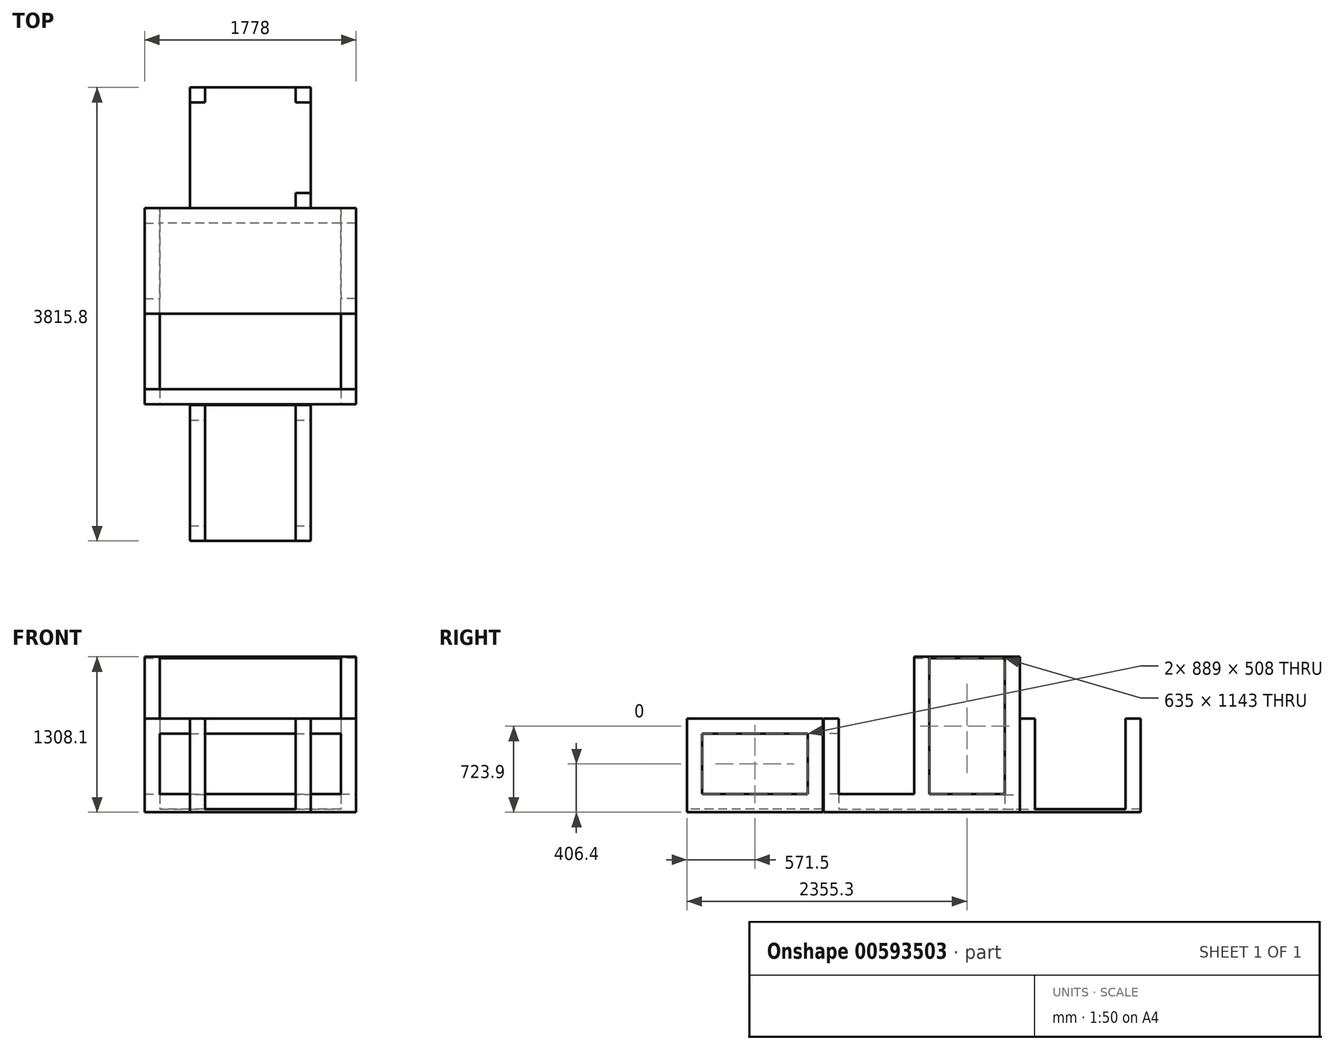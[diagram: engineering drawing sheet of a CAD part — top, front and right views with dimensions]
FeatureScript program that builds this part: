
annotation { "Feature Type Name" : "Feature", "Feature Type Description" : "" }
export const myFeature = defineFeature(function(context is Context, id is Id, definition is map)
    precondition{}
    {
        {
            var Q0;
            Q0=qCreatedBy(makeId("Top.planeOp"),FACE);
            var sketch = newSketch(context, id + "F0", { "sketchPlane" : qUnion([Q0])});
            skLineSegment(sketch, "E0.bottom", {"start": v(508, -571.5) * mm, "end": v(-508, -571.5) * mm});
            skLineSegment(sketch, "E0.top", {"start": v(508, 571.5) * mm, "end": v(-508, 571.5) * mm});
            skLineSegment(sketch, "E0.left", {"start": v(508, -571.5) * mm, "end": v(508, 571.5) * mm});
            skLineSegment(sketch, "E0.right", {"start": v(-508, -571.5) * mm, "end": v(-508, 571.5) * mm});
            skPoint(sketch, "E0.middle", {"position": v(0, 0) * mm});
            skLineSegment(sketch, "E1.bottom", {"start": v(-889, 577.3) * mm, "end": v(889, 577.3) * mm});
            skLineSegment(sketch, "E1.top", {"start": v(-889, 2228.3) * mm, "end": v(889, 2228.3) * mm});
            skLineSegment(sketch, "E1.left", {"start": v(-889, 577.3) * mm, "end": v(-889, 2228.3) * mm});
            skLineSegment(sketch, "E1.right", {"start": v(889, 577.3) * mm, "end": v(889, 2228.3) * mm});
            skSolve(sketch);
        }
        {
            var Q0;
            Q0=makeQuery(id+"F0.imprint","IMPRINT",FACE,{"disambiguationData":[TD([[makeQuery(id+"F0.imprint","IMPRINT",EDGE,{"derivedFrom":sQuery(id+"F0.wireOp",EDGE,"E1.bottom")}),1.0]])]});
            var sketch = newSketch(context, id + "F1", { "sketchPlane" : qUnion([Q0])});
            skLineSegment(sketch, "E2.bottom", {"start": v(-508, 2228.3) * mm, "end": v(508, 2228.3) * mm});
            skLineSegment(sketch, "E2.top", {"start": v(-508, 3244.3) * mm, "end": v(508, 3244.3) * mm});
            skLineSegment(sketch, "E2.left", {"start": v(-508, 2228.3) * mm, "end": v(-508, 3244.3) * mm});
            skLineSegment(sketch, "E2.right", {"start": v(508, 2228.3) * mm, "end": v(508, 3244.3) * mm});
            skSolve(sketch);
        }
        {
            var Q0;
            Q0=makeQuery(id+"F1.imprint","IMPRINT",FACE,{"disambiguationData":[TD([[makeQuery(id+"F1.imprint","IMPRINT",EDGE,{"derivedFrom":sQuery(id+"F1.wireOp",EDGE,"E2.bottom")}),1.0]])]});
            var Q1;
            Q1=makeQuery(id+"F0.imprint","IMPRINT",FACE,{"disambiguationData":[TD([[makeQuery(id+"F0.imprint","IMPRINT",EDGE,{"derivedFrom":sQuery(id+"F0.wireOp",EDGE,"E1.bottom")}),1.0]])]});
            var Q2;
            Q2=makeQuery(id+"F0.imprint","IMPRINT",FACE,{"disambiguationData":[TD([[makeQuery(id+"F0.imprint","IMPRINT",EDGE,{"derivedFrom":sQuery(id+"F0.wireOp",EDGE,"E0.bottom")}),-1.0]])]});
            extrude(context, id + "F2", {"entities" : qUnion([Q0, Q1, Q2]), "depth" : 25.4 * mm, "offsetDistance" : 25.4 * mm});
        }
        {
            var Q0;
            Q0=makeQuery(id+"F2.opExtrude","CAP_FACE",FACE,{"disambiguationData":[OSD([sQuery(id+"F0.wireOp",EDGE,"E0.bottom"),sQuery(id+"F0.wireOp",EDGE,"E0.top"),sQuery(id+"F0.wireOp",EDGE,"E0.left"),sQuery(id+"F0.wireOp",EDGE,"E0.right")])],"isStart":false});
            var sketch = newSketch(context, id + "F3", { "sketchPlane" : qUnion([Q0])});
            skLineSegment(sketch, "E3.bottom", {"start": v(-508, 571.5) * mm, "end": v(-381, 571.5) * mm});
            skLineSegment(sketch, "E3.top", {"start": v(-508, 444.5) * mm, "end": v(-381, 444.5) * mm});
            skLineSegment(sketch, "E3.left", {"start": v(-508, 571.5) * mm, "end": v(-508, 444.5) * mm});
            skLineSegment(sketch, "E3.right", {"start": v(-381, 571.5) * mm, "end": v(-381, 444.5) * mm});
            skLineSegment(sketch, "E4.bottom", {"start": v(508, 571.5) * mm, "end": v(381, 571.5) * mm});
            skLineSegment(sketch, "E4.top", {"start": v(508, 444.5) * mm, "end": v(381, 444.5) * mm});
            skLineSegment(sketch, "E4.left", {"start": v(508, 571.5) * mm, "end": v(508, 444.5) * mm});
            skLineSegment(sketch, "E4.right", {"start": v(381, 571.5) * mm, "end": v(381, 444.5) * mm});
            skSolve(sketch);
        }
        {
            var Q0;
            Q0=makeQuery(id+"F3.imprint","IMPRINT",FACE,{"disambiguationData":[TD([[makeQuery(id+"F3.imprint","IMPRINT",EDGE,{"derivedFrom":sQuery(id+"F3.wireOp",EDGE,"E4.bottom")}),1.0]])]});
            var Q1;
            Q1=makeQuery(id+"F3.imprint","IMPRINT",FACE,{"disambiguationData":[TD([[makeQuery(id+"F3.imprint","IMPRINT",EDGE,{"derivedFrom":sQuery(id+"F3.wireOp",EDGE,"E3.bottom")}),1.0]])]});
            extrude(context, id + "F4", {"entities" : qUnion([Q0, Q1]), "operationType" : NewBodyOperationType.ADD, "depth" : 762 * mm, "offsetDistance" : 25.4 * mm});
        }
        {
            var Q0;
            Q0=makeQuery(id+"F2.opExtrude","CAP_FACE",FACE,{"disambiguationData":[OSD([sQuery(id+"F0.wireOp",EDGE,"E1.bottom"),sQuery(id+"F0.wireOp",EDGE,"E1.top"),sQuery(id+"F0.wireOp",EDGE,"E1.left"),sQuery(id+"F0.wireOp",EDGE,"E1.right")])],"isStart":false});
            var sketch = newSketch(context, id + "F5", { "sketchPlane" : qUnion([Q0])});
            skLineSegment(sketch, "E5.bottom", {"start": v(889, 1339.3) * mm, "end": v(762, 1339.3) * mm});
            skLineSegment(sketch, "E5.top", {"start": v(889, 1466.3) * mm, "end": v(762, 1466.3) * mm});
            skLineSegment(sketch, "E5.left", {"start": v(889, 1339.3) * mm, "end": v(889, 1466.3) * mm});
            skLineSegment(sketch, "E5.right", {"start": v(762, 1339.3) * mm, "end": v(762, 1466.3) * mm});
            skLineSegment(sketch, "E6.bottom", {"start": v(-889, 1339.3) * mm, "end": v(-762, 1339.3) * mm});
            skLineSegment(sketch, "E6.top", {"start": v(-889, 1466.3) * mm, "end": v(-762, 1466.3) * mm});
            skLineSegment(sketch, "E6.left", {"start": v(-889, 1339.3) * mm, "end": v(-889, 1466.3) * mm});
            skLineSegment(sketch, "E6.right", {"start": v(-762, 1339.3) * mm, "end": v(-762, 1466.3) * mm});
            skLineSegment(sketch, "E7.bottom", {"start": v(-889, 2228.3) * mm, "end": v(-762, 2228.3) * mm});
            skLineSegment(sketch, "E7.top", {"start": v(-889, 2101.3) * mm, "end": v(-762, 2101.3) * mm});
            skLineSegment(sketch, "E7.left", {"start": v(-889, 2228.3) * mm, "end": v(-889, 2101.3) * mm});
            skLineSegment(sketch, "E7.right", {"start": v(-762, 2228.3) * mm, "end": v(-762, 2101.3) * mm});
            skLineSegment(sketch, "E8.bottom", {"start": v(889, 2228.3) * mm, "end": v(762, 2228.3) * mm});
            skLineSegment(sketch, "E8.top", {"start": v(889, 2101.3) * mm, "end": v(762, 2101.3) * mm});
            skLineSegment(sketch, "E8.left", {"start": v(889, 2228.3) * mm, "end": v(889, 2101.3) * mm});
            skLineSegment(sketch, "E8.right", {"start": v(762, 2228.3) * mm, "end": v(762, 2101.3) * mm});
            skSolve(sketch);
        }
        {
            var Q0;
            Q0=makeQuery(id+"F5.imprint","IMPRINT",FACE,{"disambiguationData":[TD([[makeQuery(id+"F5.imprint","IMPRINT",EDGE,{"derivedFrom":sQuery(id+"F5.wireOp",EDGE,"E5.bottom")}),-1.0]])]});
            var Q1;
            Q1=makeQuery(id+"F5.imprint","IMPRINT",FACE,{"disambiguationData":[TD([[makeQuery(id+"F5.imprint","IMPRINT",EDGE,{"derivedFrom":sQuery(id+"F5.wireOp",EDGE,"E6.bottom")}),1.0]])]});
            var Q2;
            Q2=makeQuery(id+"F5.imprint","IMPRINT",FACE,{"disambiguationData":[TD([[makeQuery(id+"F5.imprint","IMPRINT",EDGE,{"derivedFrom":sQuery(id+"F5.wireOp",EDGE,"E7.bottom")}),-1.0]])]});
            var Q3;
            Q3=makeQuery(id+"F5.imprint","IMPRINT",FACE,{"disambiguationData":[TD([[makeQuery(id+"F5.imprint","IMPRINT",EDGE,{"derivedFrom":sQuery(id+"F5.wireOp",EDGE,"E8.bottom")}),-1.0]])]});
            extrude(context, id + "F6", {"entities" : qUnion([Q0, Q1, Q2, Q3]), "operationType" : NewBodyOperationType.ADD, "depth" : 1270 * mm, "offsetDistance" : 25.4 * mm});
        }
        {
            var Q0;
            Q0=makeQuery(id+"F2.opExtrude","CAP_FACE",FACE,{"disambiguationData":[OSD([sQuery(id+"F1.wireOp",EDGE,"E2.bottom"),sQuery(id+"F1.wireOp",EDGE,"E2.top"),sQuery(id+"F1.wireOp",EDGE,"E2.left"),sQuery(id+"F1.wireOp",EDGE,"E2.right")])],"isStart":false});
            var sketch = newSketch(context, id + "F7", { "sketchPlane" : qUnion([Q0])});
            skLineSegment(sketch, "E9.bottom", {"start": v(-508, 3244.3) * mm, "end": v(-381, 3244.3) * mm});
            skLineSegment(sketch, "E9.top", {"start": v(-508, 3117.3) * mm, "end": v(-381, 3117.3) * mm});
            skLineSegment(sketch, "E9.left", {"start": v(-508, 3244.3) * mm, "end": v(-508, 3117.3) * mm});
            skLineSegment(sketch, "E9.right", {"start": v(-381, 3244.3) * mm, "end": v(-381, 3117.3) * mm});
            skLineSegment(sketch, "E10.bottom", {"start": v(508, 3244.3) * mm, "end": v(381, 3244.3) * mm});
            skLineSegment(sketch, "E10.top", {"start": v(508, 3117.3) * mm, "end": v(381, 3117.3) * mm});
            skLineSegment(sketch, "E10.left", {"start": v(508, 3244.3) * mm, "end": v(508, 3117.3) * mm});
            skLineSegment(sketch, "E10.right", {"start": v(381, 3244.3) * mm, "end": v(381, 3117.3) * mm});
            skSolve(sketch);
        }
        {
            var Q0;
            Q0=makeQuery(id+"F7.imprint","IMPRINT",FACE,{"disambiguationData":[TD([[makeQuery(id+"F7.imprint","IMPRINT",EDGE,{"derivedFrom":sQuery(id+"F7.wireOp",EDGE,"E10.bottom")}),-1.0]])]});
            var Q1;
            Q1=makeQuery(id+"F7.imprint","IMPRINT",FACE,{"disambiguationData":[TD([[makeQuery(id+"F7.imprint","IMPRINT",EDGE,{"derivedFrom":sQuery(id+"F7.wireOp",EDGE,"E9.bottom")}),-1.0]])]});
            extrude(context, id + "F8", {"entities" : qUnion([Q0, Q1]), "operationType" : NewBodyOperationType.ADD, "depth" : 762 * mm, "offsetDistance" : 25.4 * mm});
        }
        {
            var Q0;
            Q0=makeQuery(id+"F2.opExtrude","CAP_FACE",FACE,{"disambiguationData":[OSD([sQuery(id+"F1.wireOp",EDGE,"E2.bottom"),sQuery(id+"F1.wireOp",EDGE,"E2.top"),sQuery(id+"F1.wireOp",EDGE,"E2.left"),sQuery(id+"F1.wireOp",EDGE,"E2.right")])],"isStart":false});
            var sketch = newSketch(context, id + "F9", { "sketchPlane" : qUnion([Q0])});
            skLineSegment(sketch, "E11.bottom", {"start": v(-508, 2228.3) * mm, "end": v(-381, 2228.3) * mm});
            skLineSegment(sketch, "E11.top", {"start": v(-508, 2355.3) * mm, "end": v(-381, 2355.3) * mm});
            skLineSegment(sketch, "E11.left", {"start": v(-508, 2228.3) * mm, "end": v(-508, 2355.3) * mm});
            skLineSegment(sketch, "E11.right", {"start": v(-381, 2228.3) * mm, "end": v(-381, 2355.3) * mm});
            skLineSegment(sketch, "E12.bottom", {"start": v(508, 2228.3) * mm, "end": v(381, 2228.3) * mm});
            skLineSegment(sketch, "E12.top", {"start": v(508, 2355.3) * mm, "end": v(381, 2355.3) * mm});
            skLineSegment(sketch, "E12.left", {"start": v(508, 2228.3) * mm, "end": v(508, 2355.3) * mm});
            skLineSegment(sketch, "E12.right", {"start": v(381, 2228.3) * mm, "end": v(381, 2355.3) * mm});
            skSolve(sketch);
        }
        {
            var Q0;
            Q0=makeQuery(id+"F9.imprint","IMPRINT",FACE,{"disambiguationData":[TD([[makeQuery(id+"F9.imprint","IMPRINT",EDGE,{"derivedFrom":sQuery(id+"F9.wireOp",EDGE,"E11.bottom")}),1.0]])]});
            var sketch = newSketch(context, id + "F10", { "sketchPlane" : qUnion([Q0])});
            skSolve(sketch);
        }
        {
            var Q0;
            Q0 = qSketchRegion(id + "F10", true);
            var Q1;
            Q1=makeQuery(id+"F9.imprint","IMPRINT",FACE,{"disambiguationData":[TD([[makeQuery(id+"F9.imprint","IMPRINT",EDGE,{"derivedFrom":sQuery(id+"F9.wireOp",EDGE,"E12.bottom")}),1.0]])]});
            var Q2;
            Q2=makeQuery(id+"F10.imprint","IMPRINT",FACE,{"disambiguationData":[TD([[makeQuery(id+"F10.imprint","IMPRINT",EDGE,{"derivedFrom":makeQuery(id+"F9.imprint","IMPRINT",EDGE,{"derivedFrom":sQuery(id+"F9.wireOp",EDGE,"E11.bottom")})}),1.0]])]});
            extrude(context, id + "F11", {"entities" : qUnion([Q0, Q1, Q2]), "operationType" : NewBodyOperationType.ADD, "depth" : 762 * mm, "offsetDistance" : 25.4 * mm});
        }
        {
            var Q0;
            Q0=makeQuery(id+"F2.opExtrude","CAP_FACE",FACE,{"disambiguationData":[OSD([sQuery(id+"F0.wireOp",EDGE,"E0.bottom"),sQuery(id+"F0.wireOp",EDGE,"E0.top"),sQuery(id+"F0.wireOp",EDGE,"E0.left"),sQuery(id+"F0.wireOp",EDGE,"E0.right")])],"isStart":false});
            var sketch = newSketch(context, id + "F12", { "sketchPlane" : qUnion([Q0])});
            skLineSegment(sketch, "E13.bottom", {"start": v(-508, -571.5) * mm, "end": v(-381, -571.5) * mm});
            skLineSegment(sketch, "E13.top", {"start": v(-508, -444.5) * mm, "end": v(-381, -444.5) * mm});
            skLineSegment(sketch, "E13.left", {"start": v(-508, -571.5) * mm, "end": v(-508, -444.5) * mm});
            skLineSegment(sketch, "E13.right", {"start": v(-381, -571.5) * mm, "end": v(-381, -444.5) * mm});
            skLineSegment(sketch, "E14.bottom", {"start": v(508, -571.5) * mm, "end": v(381, -571.5) * mm});
            skLineSegment(sketch, "E14.top", {"start": v(508, -444.5) * mm, "end": v(381, -444.5) * mm});
            skLineSegment(sketch, "E14.left", {"start": v(508, -571.5) * mm, "end": v(508, -444.5) * mm});
            skLineSegment(sketch, "E14.right", {"start": v(381, -571.5) * mm, "end": v(381, -444.5) * mm});
            skSolve(sketch);
        }
        {
            var Q0;
            Q0=makeQuery(id+"F12.imprint","IMPRINT",FACE,{"disambiguationData":[TD([[makeQuery(id+"F12.imprint","IMPRINT",EDGE,{"derivedFrom":sQuery(id+"F12.wireOp",EDGE,"E13.bottom")}),-1.0]])]});
            var Q1;
            Q1=makeQuery(id+"F12.imprint","IMPRINT",FACE,{"disambiguationData":[TD([[makeQuery(id+"F12.imprint","IMPRINT",EDGE,{"derivedFrom":sQuery(id+"F12.wireOp",EDGE,"E14.bottom")}),-1.0]])]});
            extrude(context, id + "F13", {"entities" : qUnion([Q0, Q1]), "operationType" : NewBodyOperationType.ADD, "depth" : 762 * mm, "offsetDistance" : 25.4 * mm});
        }
        {
            var Q0;
            Q0=makeQuery(id+"F2.opExtrude","CAP_FACE",FACE,{"disambiguationData":[OSD([sQuery(id+"F0.wireOp",EDGE,"E1.bottom"),sQuery(id+"F0.wireOp",EDGE,"E1.top"),sQuery(id+"F0.wireOp",EDGE,"E1.left"),sQuery(id+"F0.wireOp",EDGE,"E1.right")])],"isStart":false});
            var sketch = newSketch(context, id + "F14", { "sketchPlane" : qUnion([Q0])});
            skLineSegment(sketch, "E15.bottom", {"start": v(-889, 577.3) * mm, "end": v(-762, 577.3) * mm});
            skLineSegment(sketch, "E15.top", {"start": v(-889, 704.3) * mm, "end": v(-762, 704.3) * mm});
            skLineSegment(sketch, "E15.left", {"start": v(-889, 577.3) * mm, "end": v(-889, 704.3) * mm});
            skLineSegment(sketch, "E15.right", {"start": v(-762, 577.3) * mm, "end": v(-762, 704.3) * mm});
            skLineSegment(sketch, "E16.bottom", {"start": v(889, 577.3) * mm, "end": v(762, 577.3) * mm});
            skLineSegment(sketch, "E16.top", {"start": v(889, 704.3) * mm, "end": v(762, 704.3) * mm});
            skLineSegment(sketch, "E16.left", {"start": v(889, 577.3) * mm, "end": v(889, 704.3) * mm});
            skLineSegment(sketch, "E16.right", {"start": v(762, 577.3) * mm, "end": v(762, 704.3) * mm});
            skSolve(sketch);
        }
        {
            var Q0;
            Q0=makeQuery(id+"F14.imprint","IMPRINT",FACE,{"disambiguationData":[TD([[makeQuery(id+"F14.imprint","IMPRINT",EDGE,{"derivedFrom":sQuery(id+"F14.wireOp",EDGE,"E15.bottom")}),1.0]])]});
            var Q1;
            Q1=makeQuery(id+"F14.imprint","IMPRINT",FACE,{"disambiguationData":[TD([[makeQuery(id+"F14.imprint","IMPRINT",EDGE,{"derivedFrom":sQuery(id+"F14.wireOp",EDGE,"E16.bottom")}),1.0]])]});
            extrude(context, id + "F15", {"entities" : qUnion([Q0, Q1]), "operationType" : NewBodyOperationType.ADD, "depth" : 762 * mm, "offsetDistance" : 25.4 * mm});
        }
        {
            var Q0;
            Q0=makeQuery(id+"F15.opExtrude","SWEPT_FACE",FACE,{"disambiguationData":[OSD([sQuery(id+"F14.wireOp",EDGE,"E16.right")])]});
            var sketch = newSketch(context, id + "F16", { "sketchPlane" : qUnion([Q0])});
            skLineSegment(sketch, "E17.bottom", {"start": v(-704.3, 787.4) * mm, "end": v(-577.3, 787.4) * mm});
            skLineSegment(sketch, "E17.top", {"start": v(-704.3, 660.4) * mm, "end": v(-577.3, 660.4) * mm});
            skLineSegment(sketch, "E17.left", {"start": v(-704.3, 787.4) * mm, "end": v(-704.3, 660.4) * mm});
            skLineSegment(sketch, "E17.right", {"start": v(-577.3, 787.4) * mm, "end": v(-577.3, 660.4) * mm});
            skSolve(sketch);
        }
        {
            var Q0;
            Q0=makeQuery(id+"F16.imprint","IMPRINT",FACE,{"disambiguationData":[TD([[makeQuery(id+"F16.imprint","IMPRINT",EDGE,{"derivedFrom":sQuery(id+"F16.wireOp",EDGE,"E17.bottom")}),1.0]])]});
            extrude(context, id + "F17", {"entities" : qUnion([Q0]), "operationType" : NewBodyOperationType.ADD, "depth" : 1524 * mm, "offsetDistance" : 25.4 * mm});
        }
        {
            var Q0;
            Q0=makeQuery(id+"F4.opExtrude","SWEPT_FACE",FACE,{"disambiguationData":[OSD([sQuery(id+"F3.wireOp",EDGE,"E3.top")])]});
            var sketch = newSketch(context, id + "F18", { "sketchPlane" : qUnion([Q0])});
            skLineSegment(sketch, "E18.bottom", {"start": v(-508, 787.4) * mm, "end": v(-381, 787.4) * mm});
            skLineSegment(sketch, "E18.top", {"start": v(-508, 660.4) * mm, "end": v(-381, 660.4) * mm});
            skLineSegment(sketch, "E18.left", {"start": v(-508, 787.4) * mm, "end": v(-508, 660.4) * mm});
            skLineSegment(sketch, "E18.right", {"start": v(-381, 787.4) * mm, "end": v(-381, 660.4) * mm});
            skLineSegment(sketch, "E19.bottom", {"start": v(381, 787.4) * mm, "end": v(508, 787.4) * mm});
            skLineSegment(sketch, "E19.top", {"start": v(381, 660.4) * mm, "end": v(508, 660.4) * mm});
            skLineSegment(sketch, "E19.left", {"start": v(381, 787.4) * mm, "end": v(381, 660.4) * mm});
            skLineSegment(sketch, "E19.right", {"start": v(508, 787.4) * mm, "end": v(508, 660.4) * mm});
            skSolve(sketch);
        }
        {
            var Q0;
            Q0=makeQuery(id+"F18.imprint","IMPRINT",FACE,{"disambiguationData":[TD([[makeQuery(id+"F18.imprint","IMPRINT",EDGE,{"derivedFrom":sQuery(id+"F18.wireOp",EDGE,"E19.bottom")}),-1.0]])]});
            var Q1;
            Q1=makeQuery(id+"F18.imprint","IMPRINT",FACE,{"disambiguationData":[TD([[makeQuery(id+"F18.imprint","IMPRINT",EDGE,{"derivedFrom":sQuery(id+"F18.wireOp",EDGE,"E18.bottom")}),-1.0]])]});
            extrude(context, id + "F19", {"entities" : qUnion([Q0, Q1]), "operationType" : NewBodyOperationType.ADD, "depth" : 889 * mm, "offsetDistance" : 25.4 * mm});
        }
        {
            var Q0;
            Q0=makeQuery(id+"F4.opExtrude","SWEPT_FACE",FACE,{"disambiguationData":[OSD([sQuery(id+"F3.wireOp",EDGE,"E3.top")])]});
            var sketch = newSketch(context, id + "F20", { "sketchPlane" : qUnion([Q0])});
            skLineSegment(sketch, "E20.bottom", {"start": v(-508, 25.4) * mm, "end": v(-381, 25.4) * mm});
            skLineSegment(sketch, "E20.top", {"start": v(-508, 152.4) * mm, "end": v(-381, 152.4) * mm});
            skLineSegment(sketch, "E20.left", {"start": v(-508, 25.4) * mm, "end": v(-508, 152.4) * mm});
            skLineSegment(sketch, "E20.right", {"start": v(-381, 25.4) * mm, "end": v(-381, 152.4) * mm});
            skLineSegment(sketch, "E21.bottom", {"start": v(381, 152.4) * mm, "end": v(508, 152.4) * mm});
            skLineSegment(sketch, "E21.top", {"start": v(381, 25.4) * mm, "end": v(508, 25.4) * mm});
            skLineSegment(sketch, "E21.left", {"start": v(381, 152.4) * mm, "end": v(381, 25.4) * mm});
            skLineSegment(sketch, "E21.right", {"start": v(508, 152.4) * mm, "end": v(508, 25.4) * mm});
            skSolve(sketch);
        }
        {
            var Q0;
            Q0=makeQuery(id+"F20.imprint","IMPRINT",FACE,{"disambiguationData":[TD([[makeQuery(id+"F20.imprint","IMPRINT",EDGE,{"derivedFrom":sQuery(id+"F20.wireOp",EDGE,"E20.bottom")}),1.0]])]});
            var Q1;
            Q1=makeQuery(id+"F20.imprint","IMPRINT",FACE,{"disambiguationData":[TD([[makeQuery(id+"F20.imprint","IMPRINT",EDGE,{"derivedFrom":sQuery(id+"F20.wireOp",EDGE,"E21.bottom")}),-1.0]])]});
            extrude(context, id + "F21", {"entities" : qUnion([Q0, Q1]), "operationType" : NewBodyOperationType.ADD, "depth" : 889 * mm, "offsetDistance" : 25.4 * mm});
        }
        {
            var Q0;
            Q0=makeQuery(id+"F2.opExtrude","CAP_FACE",FACE,{"disambiguationData":[OSD([sQuery(id+"F0.wireOp",EDGE,"E1.bottom"),sQuery(id+"F0.wireOp",EDGE,"E1.top"),sQuery(id+"F0.wireOp",EDGE,"E1.left"),sQuery(id+"F0.wireOp",EDGE,"E1.right")])],"isStart":false});
            var sketch = newSketch(context, id + "F22", { "sketchPlane" : qUnion([Q0])});
            skLineSegment(sketch, "E22.bottom", {"start": v(-762, 2101.3) * mm, "end": v(-889, 2101.3) * mm});
            skLineSegment(sketch, "E22.top", {"start": v(-762, 1466.3) * mm, "end": v(-889, 1466.3) * mm});
            skLineSegment(sketch, "E22.left", {"start": v(-762, 2101.3) * mm, "end": v(-762, 1466.3) * mm});
            skLineSegment(sketch, "E22.right", {"start": v(-889, 2101.3) * mm, "end": v(-889, 1466.3) * mm});
            skLineSegment(sketch, "E23.bottom", {"start": v(-762, 1339.3) * mm, "end": v(-889.9, 1339.3) * mm});
            skLineSegment(sketch, "E23.top", {"start": v(-762, 704.3) * mm, "end": v(-889.9, 704.3) * mm});
            skLineSegment(sketch, "E23.left", {"start": v(-762, 1339.3) * mm, "end": v(-762, 704.3) * mm});
            skLineSegment(sketch, "E23.right", {"start": v(-889.9, 1339.3) * mm, "end": v(-889.9, 704.3) * mm});
            skLineSegment(sketch, "E24.bottom", {"start": v(762, 1339.29) * mm, "end": v(889, 1339.29) * mm});
            skLineSegment(sketch, "E24.top", {"start": v(762, 704.3) * mm, "end": v(889, 704.3) * mm});
            skLineSegment(sketch, "E24.left", {"start": v(762, 1339.29) * mm, "end": v(762, 704.3) * mm});
            skLineSegment(sketch, "E24.right", {"start": v(889, 1339.29) * mm, "end": v(889, 704.3) * mm});
            skLineSegment(sketch, "E25.bottom", {"start": v(762, 2101.3) * mm, "end": v(889, 2101.3) * mm});
            skLineSegment(sketch, "E25.top", {"start": v(762, 1466.3) * mm, "end": v(889, 1466.3) * mm});
            skLineSegment(sketch, "E25.left", {"start": v(762, 2101.3) * mm, "end": v(762, 1466.3) * mm});
            skLineSegment(sketch, "E25.right", {"start": v(889, 2101.3) * mm, "end": v(889, 1466.3) * mm});
            skSolve(sketch);
        }
        {
            var Q0;
            Q0=makeQuery(id+"F22.imprint","IMPRINT",FACE,{"disambiguationData":[TD([[makeQuery(id+"F22.imprint","IMPRINT",EDGE,{"derivedFrom":sQuery(id+"F22.wireOp",EDGE,"E25.bottom")}),1.0]])]});
            var Q1;
            Q1=makeQuery(id+"F22.imprint","IMPRINT",FACE,{"disambiguationData":[TD([[makeQuery(id+"F22.imprint","IMPRINT",EDGE,{"derivedFrom":sQuery(id+"F22.wireOp",EDGE,"E24.bottom")}),-1.0]])]});
            var Q2;
            Q2=makeQuery(id+"F22.imprint","IMPRINT",FACE,{"disambiguationData":[TD([[makeQuery(id+"F22.imprint","IMPRINT",EDGE,{"derivedFrom":sQuery(id+"F22.wireOp",EDGE,"E22.bottom")}),-1.0]])]});
            var Q3;
            {var subQ5=sQuery(id+"F22.wireOp",EDGE,"E23.left");Q3=makeQuery(id+"F22.imprint","IMPRINT",FACE,{"disambiguationData":[TD([[makeQuery(id+"F22.imprint","IMPRINT",EDGE,{"derivedFrom":subQ5}),-1.0]])]});}
            extrude(context, id + "F23", {"entities" : qUnion([Q0, Q1, Q2, Q3]), "operationType" : NewBodyOperationType.ADD, "depth" : 127 * mm, "offsetDistance" : 25.4 * mm});
        }
        {
            var Q0;
            Q0=makeQuery(id+"F23.boolean.opBoolean","MERGE",FACE,{"derivedFrom":[makeQuery(id+"F6.opExtrude","SWEPT_FACE",FACE,{"disambiguationData":[OSD([sQuery(id+"F5.wireOp",EDGE,"E6.right")])]}),makeQuery(id+"F6.opExtrude","SWEPT_FACE",FACE,{"disambiguationData":[OSD([sQuery(id+"F5.wireOp",EDGE,"E7.right")])]}),makeQuery(id+"F15.opExtrude","SWEPT_FACE",FACE,{"disambiguationData":[OSD([sQuery(id+"F14.wireOp",EDGE,"E15.right")])]}),makeQuery(id+"F23.opExtrude","SWEPT_FACE",FACE,{"disambiguationData":[OSD([sQuery(id+"F22.wireOp",EDGE,"E22.left")])]}),makeQuery(id+"F23.opExtrude","SWEPT_FACE",FACE,{"disambiguationData":[OSD([sQuery(id+"F22.wireOp",EDGE,"E23.left")])]})]});
            var sketch = newSketch(context, id + "F24", { "sketchPlane" : qUnion([Q0])});
            skLineSegment(sketch, "E26.bottom", {"start": v(2101.44, 146.35) * mm, "end": v(2228.3, 146.35) * mm});
            skLineSegment(sketch, "E26.top", {"start": v(2101.44, 25.4) * mm, "end": v(2228.3, 25.4) * mm});
            skLineSegment(sketch, "E26.left", {"start": v(2101.44, 146.35) * mm, "end": v(2101.44, 25.4) * mm});
            skLineSegment(sketch, "E26.right", {"start": v(2228.3, 146.35) * mm, "end": v(2228.3, 25.4) * mm});
            skSolve(sketch);
        }
        {
            var Q0;
            Q0 = qSketchRegion(id + "F24", true);
            extrude(context, id + "F25", {"entities" : qUnion([Q0]), "depth" : 1524 * mm, "offsetDistance" : 25.4 * mm});
        }
        {
            var Q0;
            Q0=makeQuery(id+"F23.boolean.opBoolean","MERGE",FACE,{"derivedFrom":[makeQuery(id+"F6.opExtrude","SWEPT_FACE",FACE,{"disambiguationData":[OSD([sQuery(id+"F5.wireOp",EDGE,"E6.right")])]}),makeQuery(id+"F6.opExtrude","SWEPT_FACE",FACE,{"disambiguationData":[OSD([sQuery(id+"F5.wireOp",EDGE,"E7.right")])]}),makeQuery(id+"F15.opExtrude","SWEPT_FACE",FACE,{"disambiguationData":[OSD([sQuery(id+"F14.wireOp",EDGE,"E15.right")])]}),makeQuery(id+"F23.opExtrude","SWEPT_FACE",FACE,{"disambiguationData":[OSD([sQuery(id+"F22.wireOp",EDGE,"E22.left")])]}),makeQuery(id+"F23.opExtrude","SWEPT_FACE",FACE,{"disambiguationData":[OSD([sQuery(id+"F22.wireOp",EDGE,"E23.left")])]})]});
            var sketch = newSketch(context, id + "F26", { "sketchPlane" : qUnion([Q0])});
            skLineSegment(sketch, "E27.bottom", {"start": v(704.3, 152.4) * mm, "end": v(577.3, 152.4) * mm});
            skLineSegment(sketch, "E27.top", {"start": v(704.3, 25.4) * mm, "end": v(577.3, 25.4) * mm});
            skLineSegment(sketch, "E27.left", {"start": v(704.3, 152.4) * mm, "end": v(704.3, 25.4) * mm});
            skLineSegment(sketch, "E27.right", {"start": v(577.3, 152.4) * mm, "end": v(577.3, 25.4) * mm});
            skSolve(sketch);
        }
        {
            var Q0;
            Q0=makeQuery(id+"F26.imprint","IMPRINT",FACE,{"disambiguationData":[TD([[makeQuery(id+"F26.imprint","IMPRINT",EDGE,{"derivedFrom":sQuery(id+"F26.wireOp",EDGE,"E27.bottom")}),1.0]])]});
            extrude(context, id + "F27", {"entities" : qUnion([Q0]), "operationType" : NewBodyOperationType.ADD, "depth" : 1524 * mm, "offsetDistance" : 25.4 * mm});
        }
        {
            var Q0;
            Q0=makeQuery(id+"F6.opExtrude","CAP_FACE",FACE,{"disambiguationData":[OSD([sQuery(id+"F5.wireOp",EDGE,"E6.bottom"),sQuery(id+"F5.wireOp",EDGE,"E6.top"),sQuery(id+"F5.wireOp",EDGE,"E6.left"),sQuery(id+"F5.wireOp",EDGE,"E6.right")])],"isStart":false});
            var sketch = newSketch(context, id + "F28", { "sketchPlane" : qUnion([Q0])});
            skLineSegment(sketch, "E28.bottom", {"start": v(-889, 1339.3) * mm, "end": v(889, 1339.3) * mm});
            skLineSegment(sketch, "E28.top", {"start": v(-889, 2228.3) * mm, "end": v(889, 2228.3) * mm});
            skLineSegment(sketch, "E28.left", {"start": v(-889, 1339.3) * mm, "end": v(-889, 2228.3) * mm});
            skLineSegment(sketch, "E28.right", {"start": v(889, 1339.3) * mm, "end": v(889, 2228.3) * mm});
            skSolve(sketch);
        }
        {
            var Q0;
            {var subQ2=sQuery(id+"F28.wireOp",EDGE,"E28.top");Q0=makeQuery(id+"F28.imprint","IMPRINT",FACE,{"disambiguationData":[TD([[makeQuery(id+"F28.imprint","IMPRINT",EDGE,{"derivedFrom":subQ2}),-1.0]])]});}
            var Q1;
            {var subQ4=makeQuery(id+"F6.opExtrude","CAP_EDGE",EDGE,{"disambiguationData":[OSD([sQuery(id+"F5.wireOp",EDGE,"E6.top")])],"isStart":false});Q1=makeQuery(id+"F28.imprint","IMPRINT",FACE,{"disambiguationData":[TD([[makeQuery(id+"F28.imprint","IMPRINT",EDGE,{"derivedFrom":subQ4}),-1.0]])]});}
            extrude(context, id + "F29", {"entities" : qUnion([Q0, Q1]), "operationType" : NewBodyOperationType.ADD, "depth" : 12.7 * mm, "offsetDistance" : 25.4 * mm});
        }
    });
